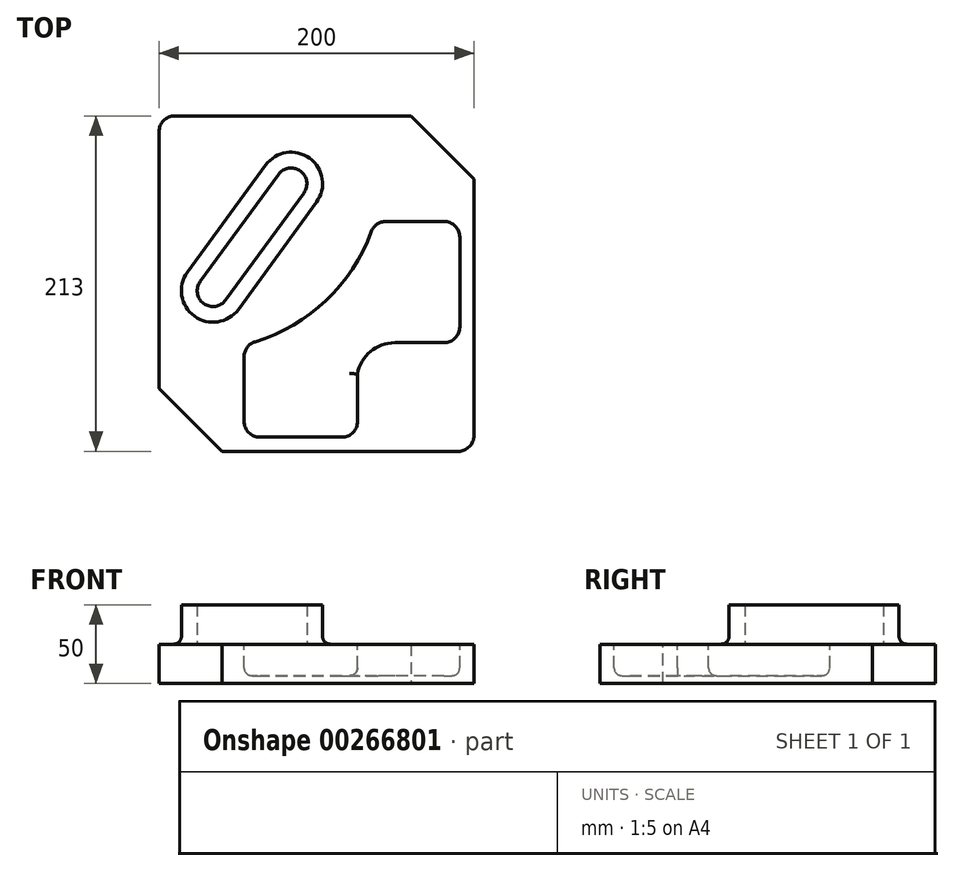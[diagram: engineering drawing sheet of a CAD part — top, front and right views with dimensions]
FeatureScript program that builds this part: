
annotation { "Feature Type Name" : "Feature", "Feature Type Description" : "" }
export const myFeature = defineFeature(function(context is Context, id is Id, definition is map)
    precondition{}
    {
        {
            var Q0;
            Q0=qCreatedBy(makeId("Top.planeOp"),FACE);
            var sketch = newSketch(context, id + "F0", { "sketchPlane" : qUnion([Q0])});
            skLineSegment(sketch, "E0.bottom", {"start": v(-100, -106.5) * mm, "end": v(100, -106.5) * mm});
            skLineSegment(sketch, "E0.top", {"start": v(-100, 106.5) * mm, "end": v(100, 106.5) * mm});
            skLineSegment(sketch, "E0.left", {"start": v(-100, -106.5) * mm, "end": v(-100, 106.5) * mm});
            skLineSegment(sketch, "E0.right", {"start": v(100, -106.5) * mm, "end": v(100, 106.5) * mm});
            skPoint(sketch, "E0.middle", {"position": v(0, 0) * mm});
            skSolve(sketch);
        }
        {
            var Q0;
            Q0 = qSketchRegion(id + "F0", true);
            extrude(context, id + "F1", {"entities" : qUnion([Q0]), "depth" : 25 * mm});
        }
        {
            var Q0;
            Q0=makeQuery(id+"F1.opExtrude","SWEPT_EDGE",EDGE,{"disambiguationData":[OSD([sQuery(id+"F0.wireOp",EDGE,"E0.top"),sQuery(id+"F0.wireOp",EDGE,"E0.right")])]});
            var Q1;
            Q1=makeQuery(id+"F1.opExtrude","SWEPT_EDGE",EDGE,{"disambiguationData":[OSD([sQuery(id+"F0.wireOp",EDGE,"E0.bottom"),sQuery(id+"F0.wireOp",EDGE,"E0.left")])]});
            chamfer(context, id + "F2", {"entities" : qUnion([Q0, Q1]), "width" : 40 * mm, "tangentPropagation" : true});
        }
        {
            var Q0;
            Q0=makeQuery(id+"F1.opExtrude","SWEPT_EDGE",EDGE,{"disambiguationData":[OSD([sQuery(id+"F0.wireOp",EDGE,"E0.top"),sQuery(id+"F0.wireOp",EDGE,"E0.left")])]});
            var Q1;
            Q1=makeQuery(id+"F1.opExtrude","SWEPT_EDGE",EDGE,{"disambiguationData":[OSD([sQuery(id+"F0.wireOp",EDGE,"E0.bottom"),sQuery(id+"F0.wireOp",EDGE,"E0.right")])]});
            fillet(context, id + "F3", {"entities" : qUnion([Q0, Q1]), "radius" : 10 * mm, "tangentPropagation" : true, "allowEdgeOverflow" : false});
        }
        {
            var Q0;
            Q0=makeQuery(id+"F1.opExtrude","CAP_FACE",FACE,{"disambiguationData":[OSD([sQuery(id+"F0.wireOp",EDGE,"E0.bottom"),sQuery(id+"F0.wireOp",EDGE,"E0.top"),sQuery(id+"F0.wireOp",EDGE,"E0.left"),sQuery(id+"F0.wireOp",EDGE,"E0.right")])],"isStart":false});
            var sketch = newSketch(context, id + "F4", { "sketchPlane" : qUnion([Q0])});
            skLineSegment(sketch, "E1", {"start": v(-32.3, 75.3) * mm, "end": v(-81.95, 7.3) * mm});
            skLineSegment(sketch, "E2", {"start": v(-49.64, -16.3) * mm, "end": v(0, 51.7) * mm});
            skArc(sketch, "E3", {"start": v(-81.95, 7.3) * mm, "mid": v(-77.59, -20.65) * mm, "end": v(-49.64, -16.3) * mm});
            skArc(sketch, "E4", {"start": v(0, 51.7) * mm, "mid": v(-4.36, 79.65) * mm, "end": v(-32.3, 75.3) * mm});
            skLineSegment(sketch, "E5", {"start": v(-24.23, 69.4) * mm, "end": v(-73.87, 1.4) * mm});
            skLineSegment(sketch, "E6", {"start": v(-57.72, -10.4) * mm, "end": v(-8.08, 57.6) * mm});
            skArc(sketch, "E7", {"start": v(-8.08, 57.6) * mm, "mid": v(-10.26, 71.58) * mm, "end": v(-24.23, 69.4) * mm});
            skArc(sketch, "E8", {"start": v(-73.87, 1.4) * mm, "mid": v(-71.7, -12.58) * mm, "end": v(-57.72, -10.4) * mm});
            skSolve(sketch);
        }
        {
            var Q0;
            Q0=makeQuery(id+"F4.imprint","IMPRINT",FACE,{"disambiguationData":[TD([[makeQuery(id+"F4.imprint","IMPRINT",EDGE,{"derivedFrom":sQuery(id+"F4.wireOp",EDGE,"E1")}),1.0]])]});
            extrude(context, id + "F5", {"entities" : qUnion([Q0]), "operationType" : NewBodyOperationType.ADD, "depth" : 50 * mm, "symmetric" : true});
        }
        {
            var Q0;
            Q0=makeQuery(id+"F5.boolean.opBoolean","INTERSECT",EDGE,{"derivedFrom":[makeQuery(id+"F1.opExtrude","CAP_FACE",FACE,{"disambiguationData":[OSD([sQuery(id+"F0.wireOp",EDGE,"E0.bottom"),sQuery(id+"F0.wireOp",EDGE,"E0.top"),sQuery(id+"F0.wireOp",EDGE,"E0.left"),sQuery(id+"F0.wireOp",EDGE,"E0.right")])],"isStart":false}),makeQuery(id+"F5.opExtrude","SWEPT_FACE",FACE,{"disambiguationData":[OSD([sQuery(id+"F4.wireOp",EDGE,"E2")])]})]});
            fillet(context, id + "F6", {"entities" : qUnion([Q0]), "radius" : 5 * mm, "tangentPropagation" : true, "allowEdgeOverflow" : false});
        }
        {
            var Q0;
            {var subQ0=sQuery(id+"F0.wireOp",EDGE,"E0.top");var subQ1=sQuery(id+"F0.wireOp",EDGE,"E0.left");var subQ2=sQuery(id+"F0.wireOp",EDGE,"E0.right");var subQ3=sQuery(id+"F0.wireOp",EDGE,"E0.bottom");Q0=makeQuery(id+"F5.boolean.opBoolean","SPLIT",FACE,{"disambiguationData":[TD([makeQuery(id+"F1.opExtrude","SWEPT_FACE",FACE,{"disambiguationData":[OSD([subQ3])]})])],"derivedFrom":makeQuery(id+"F1.opExtrude","CAP_FACE",FACE,{"disambiguationData":[OSD([subQ3,subQ0,subQ1,subQ2])],"isStart":false})});}
            var sketch = newSketch(context, id + "F7", { "sketchPlane" : qUnion([Q0])});
            skLineSegment(sketch, "E9", {"start": v(91, 39.5) * mm, "end": v(91, -37.5) * mm});
            skLineSegment(sketch, "E10", {"start": v(91, -37.5) * mm, "end": v(49.7, -37.5) * mm});
            skLineSegment(sketch, "E11", {"start": v(91, 39.5) * mm, "end": v(36.94, 39.5) * mm});
            skArc(sketch, "E12", {"start": v(49.7, -37.5) * mm, "mid": v(34.24, -43.14) * mm, "end": v(26.05, -57.4) * mm});
            skLineSegment(sketch, "E13", {"start": v(26.05, -57.4) * mm, "end": v(26.05, -97.5) * mm});
            skLineSegment(sketch, "E14", {"start": v(26.05, -97.5) * mm, "end": v(-46, -97.5) * mm});
            skLineSegment(sketch, "E15", {"start": v(-46, -97.5) * mm, "end": v(-46, -38.84) * mm});
            skArc(sketch, "E16", {"start": v(-46, -38.84) * mm, "mid": v(5.97, -10.8) * mm, "end": v(36.94, 39.5) * mm});
            skSolve(sketch);
        }
        {
            var Q0;
            Q0 = qSketchRegion(id + "F7", true);
            extrude(context, id + "F8", {"entities" : qUnion([Q0]), "operationType" : NewBodyOperationType.REMOVE, "oppositeDirection" : true, "depth" : 20 * mm});
        }
        {
            var Q0;
            Q0=makeQuery(id+"F8.boolean.opBoolean","COPY",EDGE,{"derivedFrom":makeQuery(id+"F8.opExtrude","SWEPT_EDGE",EDGE,{"disambiguationData":[OSD([sQuery(id+"F7.wireOp",EDGE,"E11"),sQuery(id+"F7.wireOp",EDGE,"E16")])]})});
            var Q1;
            Q1=makeQuery(id+"F8.boolean.opBoolean","COPY",EDGE,{"derivedFrom":makeQuery(id+"F8.opExtrude","SWEPT_EDGE",EDGE,{"disambiguationData":[OSD([sQuery(id+"F7.wireOp",EDGE,"E9"),sQuery(id+"F7.wireOp",EDGE,"E11")])]})});
            var Q2;
            Q2=makeQuery(id+"F8.boolean.opBoolean","COPY",EDGE,{"derivedFrom":makeQuery(id+"F8.opExtrude","SWEPT_EDGE",EDGE,{"disambiguationData":[OSD([sQuery(id+"F7.wireOp",EDGE,"E9"),sQuery(id+"F7.wireOp",EDGE,"E10")])]})});
            var Q3;
            Q3=makeQuery(id+"F8.boolean.opBoolean","COPY",EDGE,{"derivedFrom":makeQuery(id+"F8.opExtrude","SWEPT_EDGE",EDGE,{"disambiguationData":[OSD([sQuery(id+"F7.wireOp",EDGE,"E15"),sQuery(id+"F7.wireOp",EDGE,"E16")])]})});
            var Q4;
            Q4=makeQuery(id+"F8.boolean.opBoolean","COPY",EDGE,{"derivedFrom":makeQuery(id+"F8.opExtrude","SWEPT_EDGE",EDGE,{"disambiguationData":[OSD([sQuery(id+"F7.wireOp",EDGE,"E14"),sQuery(id+"F7.wireOp",EDGE,"E15")])]})});
            var Q5;
            Q5=makeQuery(id+"F8.boolean.opBoolean","COPY",EDGE,{"derivedFrom":makeQuery(id+"F8.opExtrude","SWEPT_EDGE",EDGE,{"disambiguationData":[OSD([sQuery(id+"F7.wireOp",EDGE,"E13"),sQuery(id+"F7.wireOp",EDGE,"E14")])]})});
            fillet(context, id + "F9", {"entities" : qUnion([Q0, Q1, Q2, Q3, Q4, Q5]), "radius" : 10 * mm, "tangentPropagation" : true, "allowEdgeOverflow" : false});
        }
        {
            var Q0;
            Q0=makeQuery(id+"F8.boolean.opBoolean","COPY",EDGE,{"derivedFrom":makeQuery(id+"F8.opExtrude","CAP_EDGE",EDGE,{"disambiguationData":[OSD([sQuery(id+"F7.wireOp",EDGE,"E16")])],"isStart":false})});
            var Q1;
            Q1=makeQuery(id+"F8.boolean.opBoolean","COPY",EDGE,{"derivedFrom":makeQuery(id+"F8.opExtrude","CAP_EDGE",EDGE,{"disambiguationData":[OSD([sQuery(id+"F7.wireOp",EDGE,"E16")])],"isStart":true})});
            var Q2;
            {var subQ0=sQuery(id+"F7.wireOp",EDGE,"E11");Q2=makeQuery(id+"F9.opFillet","BLEND_EDGE",EDGE,{"blendedFrom":[makeQuery(id+"F8.boolean.opBoolean","COPY",EDGE,{"derivedFrom":makeQuery(id+"F8.opExtrude","SWEPT_EDGE",EDGE,{"disambiguationData":[OSD([subQ0,sQuery(id+"F7.wireOp",EDGE,"E16")])]})}),makeQuery(id+"F8.boolean.opBoolean","COPY",FACE,{"derivedFrom":makeQuery(id+"F8.opExtrude","SWEPT_FACE",FACE,{"disambiguationData":[OSD([subQ0])]})})],"blendedInto":[makeQuery(id+"F8.boolean.opBoolean","COPY",FACE,{"derivedFrom":makeQuery(id+"F8.opExtrude","SWEPT_FACE",FACE,{"disambiguationData":[OSD([subQ0])]})})]});}
            var Q3;
            {var subQ0=sQuery(id+"F7.wireOp",EDGE,"E16");Q3=makeQuery(id+"F9.opFillet","BLEND_EDGE",EDGE,{"blendedFrom":[makeQuery(id+"F8.boolean.opBoolean","COPY",EDGE,{"derivedFrom":makeQuery(id+"F8.opExtrude","SWEPT_EDGE",EDGE,{"disambiguationData":[OSD([sQuery(id+"F7.wireOp",EDGE,"E11"),subQ0])]})}),makeQuery(id+"F8.boolean.opBoolean","COPY",FACE,{"derivedFrom":makeQuery(id+"F8.opExtrude","SWEPT_FACE",FACE,{"disambiguationData":[OSD([subQ0])]})})],"blendedInto":[makeQuery(id+"F8.boolean.opBoolean","COPY",FACE,{"derivedFrom":makeQuery(id+"F8.opExtrude","SWEPT_FACE",FACE,{"disambiguationData":[OSD([subQ0])]})})]});}
            fillet(context, id + "F10", {"entities" : qUnion([Q0, Q1, Q2, Q3]), "radius" : 5 * mm, "tangentPropagation" : true, "allowEdgeOverflow" : false});
        }
    });
